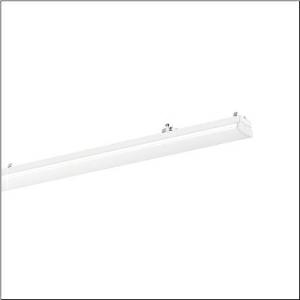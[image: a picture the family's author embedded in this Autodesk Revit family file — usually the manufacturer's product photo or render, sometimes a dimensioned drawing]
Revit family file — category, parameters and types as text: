
# Revit family: licross_r__21_recessed_opal_mo_52te1dvn445g_e066
name_source: partatom
category: Lighting Fixtures
units: mm (PartAtom-declared; Revit-internal decimal feet)

## family parameters
Cut with Voids When Loaded = No
Host = Face
Light Source = No
Part Type = Normal
Room Calculation Point = No
Round Connector Dimension = Use Diameter
Shared = No

## types (1)
- --- (1 x LED, 4500 lm, 25.8 W, 4000K)
    Apparent Load = 26 VA
    CIE Flux Codes = 44 73 91 87 100
    Color Rendering = 80
    Color Temperature = 4000K
    Default Elevation = 1800 mm
    Description = Licross® 21 recessed opal MO, luminaire insert, of sheet steel, galvanised, coil coated, white, length: 1.500mm, width: 66mm, height: 67mm, LED rated luminous flux: 4.500lm, light colour: 840, control gear: DALI 2, CLO, with plug, 5-pole, with phase selection, mains connection: 220..240V, AC, 50/60Hz, start of lifetime: 26W, end of service life: 30W, internal wiring halogen-free, primary optical cover: cover, of PMMA, light emission: direct with ceiling illumination distribution, primary light characteristic: symmetric, protection rating (complete): IP54, insulation class (complete): insulation class I (protective earthing), certification: CE, ENEC, VDE, UKCA, protection symbol: D if used in an environment with non-conductive dust loads with corresponding accessories, impact resistance: IK06, permissible ambient temperature for indoor applications: -25..+45°C, corresponds to IFS (International Featured Standards) requirements for safety and quality in the food industry, reducing of maximum allowable ambient temperature of 5°C with ceiling mounting, LABS conformity tested according to VDMA 24364:2018-05, packaging unit: 1 piece
    Height = 83 mm
    Lamp = 1 x LED
    Lamp Light Flux = 4500 lm
    Lamp Power = 25.8 W
    Lamp count = 1
    Length = 1500 mm
    Luminous efficacy = 174 lm/W
    Manufacturer = Siteco
    ModVariant = No
    Model = 52TE1DVN445G
    Mounting Place = Ceiling
    Mounting Type = Pendant
    Number of Poles = 1
    OnlyDefault = Yes
    Power Factor = 1
    Product Name = Licross® 21 recessed opal MO
    Product group = luminaire insert | ceiling pendant
    ProductGroupID = 902
    Protection Class = Protection class I
    Protection Degree = IP 54
    RLX_Detail_Level = 1
    RLX_Emergency_Light_Flux = 0 lm
    RLX_Emergency_Type = 0
    RLX_Emergency_Type_DB = No
    RlxData = <blob elided: 26345 chars, md5=b65106f7>
    Socket = socket
    Standby Power = 0 W
    System Light Flux = 4500 lm
    System Power = 26 W
    Type Comments = factory setting: luminous flux: 100 % | dim-lin: 254 | 172 mA
    Type Image = l_1313666.jpg
    URL = http://relux.com
    VarID = @adj_089725
    Voltage = 0 V
    Weight = 0.00 kg
    Width = 76 mm

## geometry (parser evidence)
native form markers: Blend x4, Sweep x14
no freeform markers — native parametric forms only
